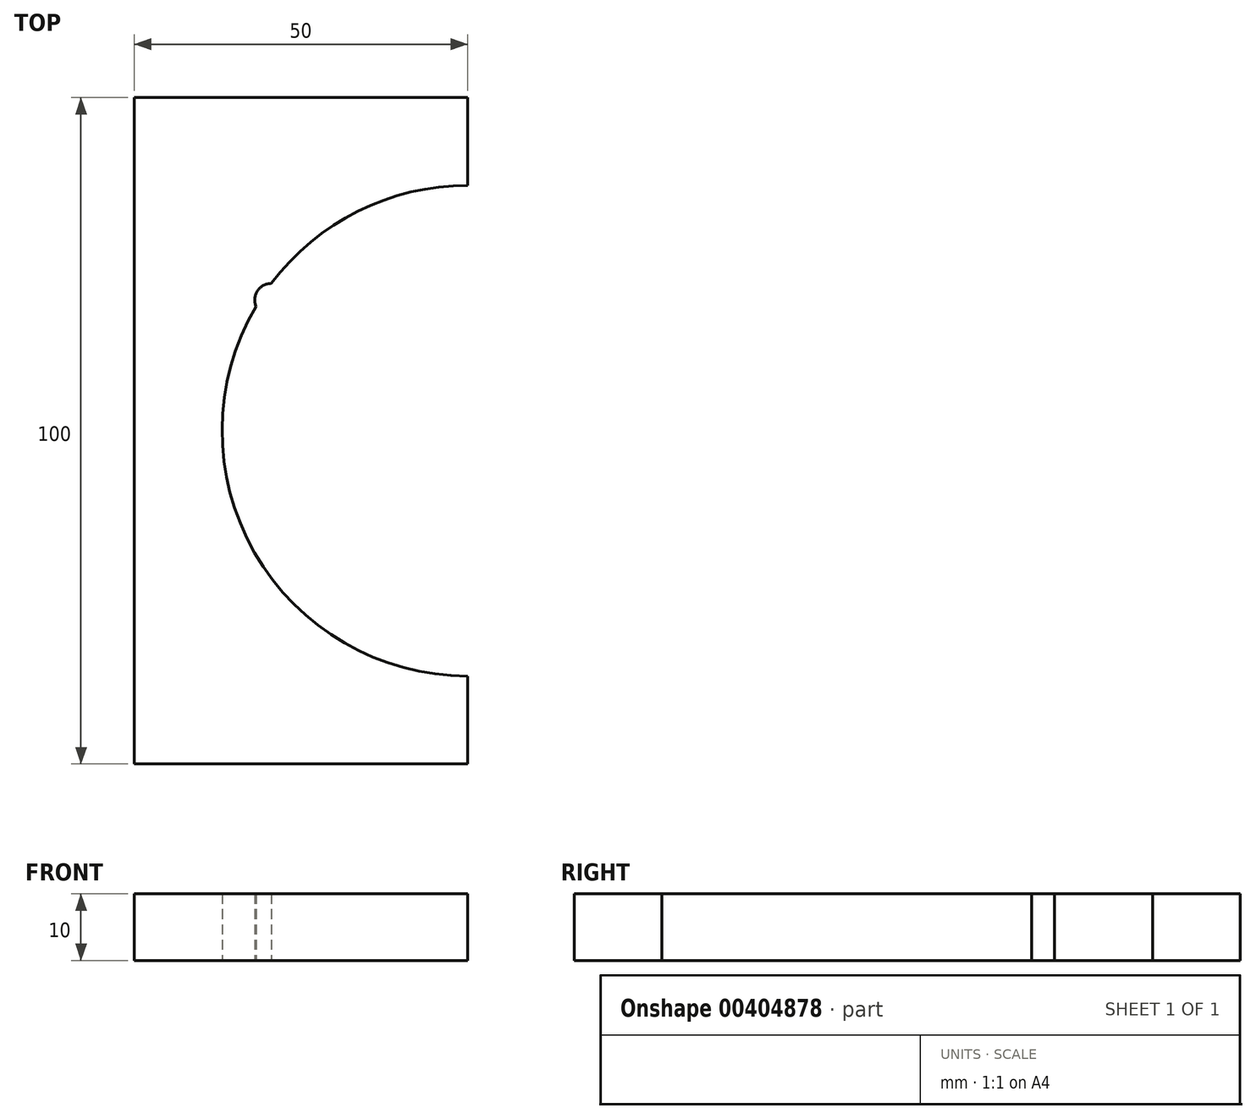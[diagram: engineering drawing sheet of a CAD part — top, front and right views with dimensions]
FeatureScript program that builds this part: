
annotation { "Feature Type Name" : "Feature", "Feature Type Description" : "" }
export const myFeature = defineFeature(function(context is Context, id is Id, definition is map)
    precondition{}
    {
        {
            var Q0;
            Q0=qCreatedBy(makeId("Top.planeOp"),FACE);
            var sketch = newSketch(context, id + "F0", { "sketchPlane" : qUnion([Q0])});
            skLineSegment(sketch, "E0.bottom", {"start": v(-51.25, -46.6) * mm, "end": v(-1.25, -46.6) * mm});
            skLineSegment(sketch, "E0.top", {"start": v(-51.25, 53.4) * mm, "end": v(-1.25, 53.4) * mm});
            skLineSegment(sketch, "E0.left", {"start": v(-51.25, -46.6) * mm, "end": v(-51.25, 53.4) * mm});
            skLineSegment(sketch, "E0.right", {"start": v(-1.25, -46.6) * mm, "end": v(-1.25, 53.4) * mm});
            skCircle(sketch, "E1", {"center": v(-30.69, 23.02) * mm, "radius": 2.5 * mm});
            skCircle(sketch, "E2", {"center": v(-1.25, 3.4) * mm, "radius": 36.82 * mm});
            skSolve(sketch);
        }
        {
            var Q0;
            Q0=makeQuery(id+"F0.imprint","IMPRINT",FACE,{"disambiguationData":[TD([[makeQuery(id+"F0.imprint","IMPRINT",EDGE,{"derivedFrom":sQuery(id+"F0.wireOp",EDGE,"E0.bottom")}),1.0]])]});
            extrude(context, id + "F1", {"entities" : qUnion([Q0]), "depth" : 10 * mm});
        }
    });
